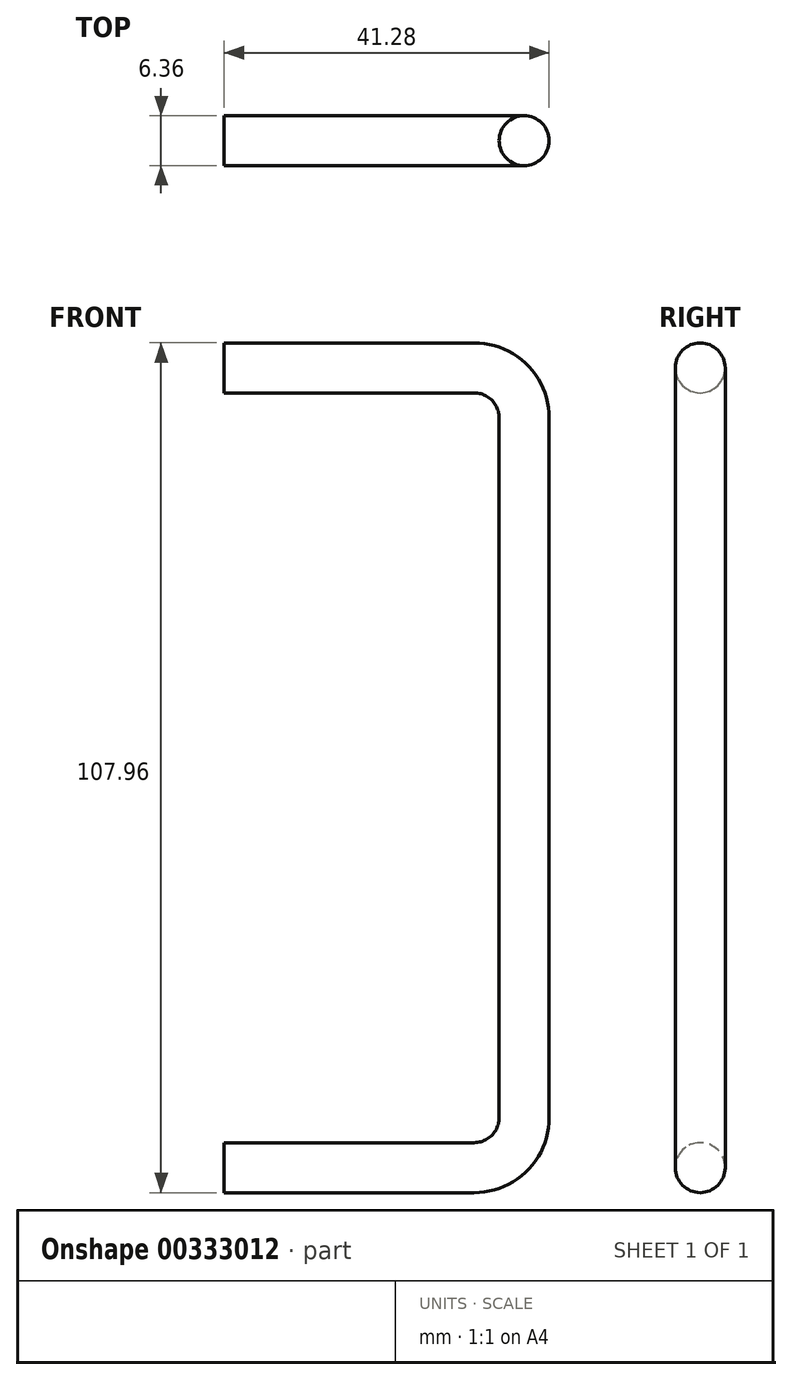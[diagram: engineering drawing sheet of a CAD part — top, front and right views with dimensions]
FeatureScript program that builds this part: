
annotation { "Feature Type Name" : "Feature", "Feature Type Description" : "" }
export const myFeature = defineFeature(function(context is Context, id is Id, definition is map)
    precondition{}
    {
        {
            var Q0;
            Q0=qCreatedBy(makeId("Front.planeOp"),FACE);
            var sketch = newSketch(context, id + "F0", { "sketchPlane" : qUnion([Q0])});
            skLineSegment(sketch, "E0", {"start": v(0, 0) * mm, "end": v(31.75, 0) * mm});
            skLineSegment(sketch, "E1", {"start": v(38.1, 6.35) * mm, "end": v(38.1, 95.25) * mm});
            skLineSegment(sketch, "E2", {"start": v(31.75, 101.6) * mm, "end": v(0, 101.6) * mm});
            skPoint(sketch, "E3.visualSharp", {"position": v(38.1, 101.6) * mm});
            skArc(sketch, "E3.filletArc", {"start": v(38.1, 95.25) * mm, "mid": v(36.24, 99.74) * mm, "end": v(31.75, 101.6) * mm});
            skPoint(sketch, "E4.visualSharp", {"position": v(38.1, 0) * mm});
            skArc(sketch, "E4.filletArc", {"start": v(31.75, 0) * mm, "mid": v(36.24, 1.86) * mm, "end": v(38.1, 6.35) * mm});
            skSolve(sketch);
        }
        {
            var Q0;
            Q0=qCreatedBy(makeId("Right.planeOp"),FACE);
            var sketch = newSketch(context, id + "F1", { "sketchPlane" : qUnion([Q0])});
            skCircle(sketch, "E5", {"center": v(0, 101.6) * mm, "radius": 3.17 * mm});
            skSolve(sketch);
        }
        {
            var Q0;
            Q0=makeQuery(id+"F1.imprint","IMPRINT",FACE,{"disambiguationData":[TD([[makeQuery(id+"F1.imprint","IMPRINT",EDGE,{"derivedFrom":sQuery(id+"F1.wireOp",EDGE,"E5")}),1.0]])]});
            var Q1;
            Q1=sQuery(id+"F0.wireOp",EDGE,"E2");
            var Q2;
            Q2=sQuery(id+"F0.wireOp",EDGE,"E3.filletArc");
            var Q3;
            Q3=sQuery(id+"F0.wireOp",EDGE,"E1");
            var Q4;
            Q4=sQuery(id+"F0.wireOp",EDGE,"E4.filletArc");
            var Q5;
            Q5=sQuery(id+"F0.wireOp",EDGE,"E0");
            sweep(context, id + "F2", {"profiles" : qUnion([Q0]), "path" : qUnion([Q1, Q2, Q3, Q4, Q5])});
        }
    });
